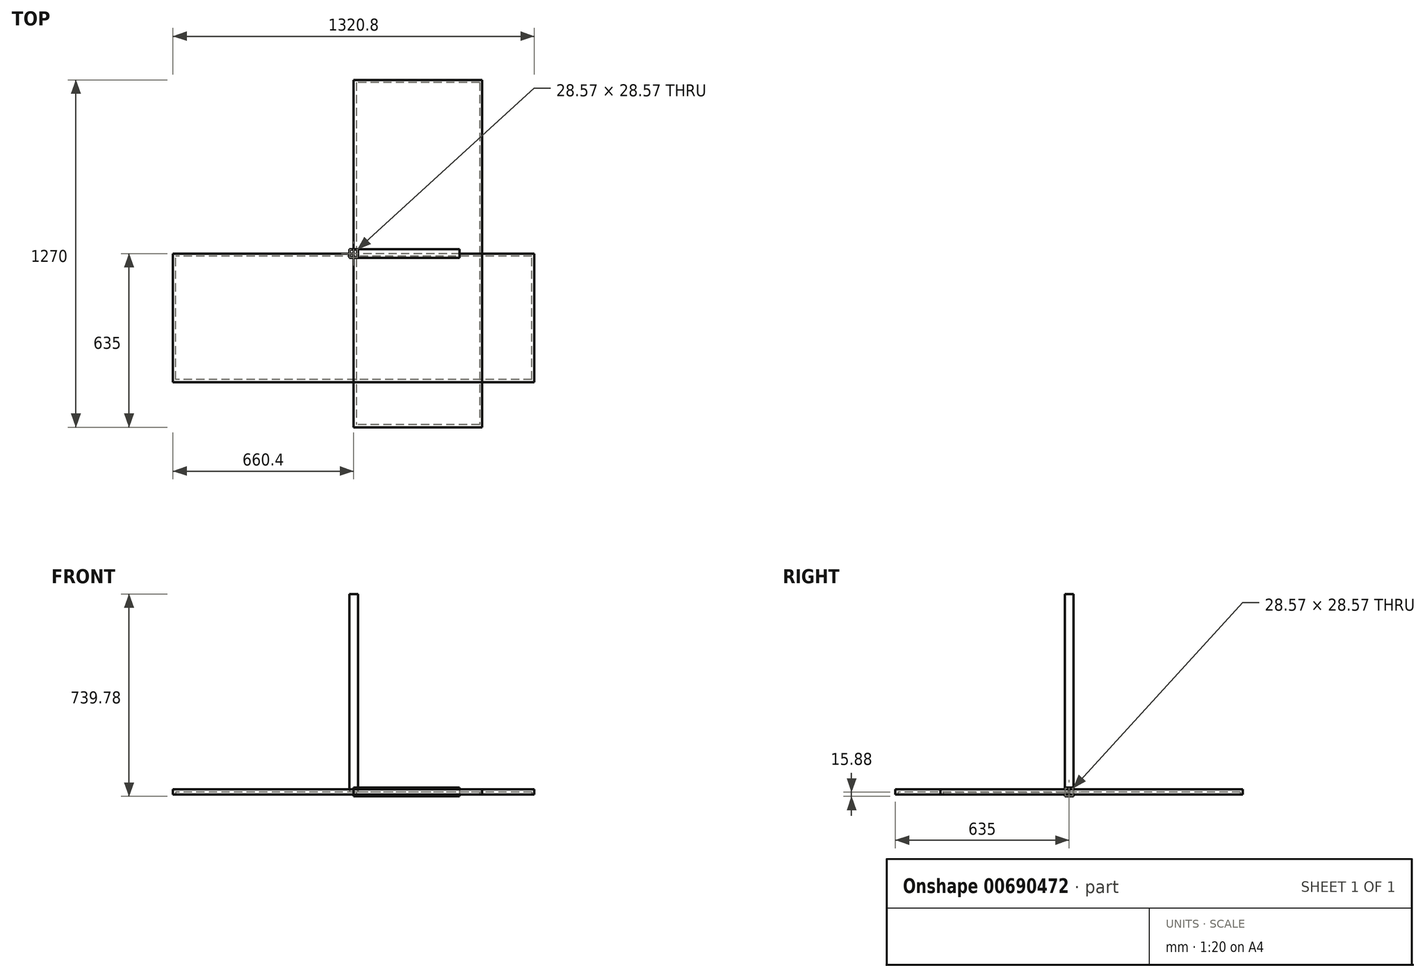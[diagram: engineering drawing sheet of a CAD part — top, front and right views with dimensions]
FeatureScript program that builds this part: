
annotation { "Feature Type Name" : "Feature", "Feature Type Description" : "" }
export const myFeature = defineFeature(function(context is Context, id is Id, definition is map)
    precondition{}
    {
        {
            var Q0;
            Q0=qCreatedBy(makeId("Front.planeOp"),FACE);
            var sketch = newSketch(context, id + "F0", { "sketchPlane" : qUnion([Q0])});
            skLineSegment(sketch, "E0.bottom", {"start": v(660.4, 9.52) * mm, "end": v(-660.4, 9.52) * mm});
            skLineSegment(sketch, "E0.top", {"start": v(650.88, -9.53) * mm, "end": v(-660.4, -9.53) * mm});
            skLineSegment(sketch, "E0.left", {"start": v(660.4, 9.52) * mm, "end": v(660.4, 0) * mm});
            skLineSegment(sketch, "E0.right", {"start": v(-660.4, 9.52) * mm, "end": v(-660.4, -9.53) * mm});
            skPoint(sketch, "E0.middle", {"position": v(0, 0) * mm});
            skPoint(sketch, "E1.orphan", {"position": v(660.4, -9.53) * mm});
            skLineSegment(sketch, "E2", {"start": v(650.88, -9.53) * mm, "end": v(660.4, -9.53) * mm});
            skLineSegment(sketch, "E3", {"start": v(660.4, 0) * mm, "end": v(660.4, -9.53) * mm});
            skSolve(sketch);
        }
        {
            var Q0;
            Q0 = qSketchRegion(id + "F0", true);
            extrude(context, id + "F1", {"entities" : qUnion([Q0]), "depth" : 469.9 * mm, "offsetDistance" : 25.4 * mm});
        }
        {
            var Q0;
            Q0=qCreatedBy(makeId("Right.planeOp"),FACE);
            var sketch = newSketch(context, id + "F2", { "sketchPlane" : qUnion([Q0])});
            skLineSegment(sketch, "E4.bottom", {"start": v(635, 9.53) * mm, "end": v(-635, 9.53) * mm});
            skLineSegment(sketch, "E4.top", {"start": v(635, -9.53) * mm, "end": v(-635, -9.53) * mm});
            skLineSegment(sketch, "E4.left", {"start": v(635, 9.52) * mm, "end": v(635, -9.53) * mm});
            skLineSegment(sketch, "E4.right", {"start": v(-635, 9.53) * mm, "end": v(-635, -9.53) * mm});
            skPoint(sketch, "E4.middle", {"position": v(0, 0) * mm});
            skLineSegment(sketch, "E5", {"start": v(-635, 9.53) * mm, "end": v(-165.1, 9.53) * mm});
            skLineSegment(sketch, "E6", {"start": v(-165.1, 9.53) * mm, "end": v(-165.1, 9.53) * mm});
            skLineSegment(sketch, "E7", {"start": v(-635, 9.53) * mm, "end": v(-635, 0) * mm});
            skLineSegment(sketch, "E8", {"start": v(-165.1, 9.53) * mm, "end": v(-165.1, 0) * mm});
            skLineSegment(sketch, "E9", {"start": v(-635, 0) * mm, "end": v(-165.1, 0) * mm});
            skSolve(sketch);
        }
        {
            var Q0;
            Q0 = qSketchRegion(id + "F2", true);
            extrude(context, id + "F3", {"entities" : qUnion([Q0]), "depth" : 469.9 * mm, "offsetDistance" : 25.4 * mm});
        }
        {
            var Q0;
            Q0=makeQuery(id+"F1.opExtrude","SWEPT_FACE",FACE,{"disambiguationData":[OSD([sQuery(id+"F0.wireOp",EDGE,"E0.top"),sQuery(id+"F0.wireOp",EDGE,"E2")])]});
            shell(context, id + "F4", {"entities" : qUnion([Q0]), "thickness" : 9.52 * mm});
        }
        {
            var Q0;
            Q0=makeQuery(id+"F3.opExtrude","SWEPT_FACE",FACE,{"disambiguationData":[OSD([sQuery(id+"F2.wireOp",EDGE,"E4.top")])]});
            var Q1;
            Q1=makeQuery(id+"F3.opExtrude","SWEPT_BODY",BODY,{"disambiguationData":[OSD([sQuery(id+"F2.wireOp",EDGE,"E4.bottom"),sQuery(id+"F2.wireOp",EDGE,"E4.top"),sQuery(id+"F2.wireOp",EDGE,"E4.left"),sQuery(id+"F2.wireOp",EDGE,"E4.right"),sQuery(id+"F2.wireOp",EDGE,"E5"),sQuery(id+"F2.wireOp",EDGE,"E7")])]});
            shell(context, id + "F5", {"entities" : qUnion([Q0]), "parts" : qUnion([Q1]), "thickness" : 9.52 * mm});
        }
        {
            var Q0;
            Q0=qCreatedBy(makeId("Top.planeOp"),FACE);
            var sketch = newSketch(context, id + "F6", { "sketchPlane" : qUnion([Q0])});
            skLineSegment(sketch, "E10.bottom", {"start": v(15.88, 15.88) * mm, "end": v(-15.88, 15.87) * mm});
            skLineSegment(sketch, "E10.top", {"start": v(15.88, -15.87) * mm, "end": v(-15.88, -15.88) * mm});
            skLineSegment(sketch, "E10.left", {"start": v(15.88, 15.88) * mm, "end": v(15.88, -15.87) * mm});
            skLineSegment(sketch, "E10.right", {"start": v(-15.88, 15.87) * mm, "end": v(-15.88, -15.88) * mm});
            skPoint(sketch, "E10.middle", {"position": v(0, 0) * mm});
            skLineSegment(sketch, "E11.bottom", {"start": v(14.29, 14.29) * mm, "end": v(-14.29, 14.29) * mm});
            skLineSegment(sketch, "E11.top", {"start": v(14.29, -14.29) * mm, "end": v(-14.29, -14.29) * mm});
            skLineSegment(sketch, "E11.left", {"start": v(14.29, 14.29) * mm, "end": v(14.29, -14.29) * mm});
            skLineSegment(sketch, "E11.right", {"start": v(-14.29, 14.29) * mm, "end": v(-14.29, -14.29) * mm});
            skSolve(sketch);
        }
        {
            var Q0;
            Q0 = qSketchRegion(id + "F6", true);
            extrude(context, id + "F7", {"entities" : qUnion([Q0]), "depth" : 723.9 * mm, "offsetDistance" : 25.4 * mm});
        }
        {
            var Q0;
            Q0=qCreatedBy(makeId("Right.planeOp"),FACE);
            var sketch = newSketch(context, id + "F8", { "sketchPlane" : qUnion([Q0])});
            skLineSegment(sketch, "E12.bottom", {"start": v(15.87, 15.88) * mm, "end": v(-15.88, 15.87) * mm});
            skLineSegment(sketch, "E12.top", {"start": v(15.88, -15.87) * mm, "end": v(-15.87, -15.88) * mm});
            skLineSegment(sketch, "E12.left", {"start": v(15.87, 15.88) * mm, "end": v(15.88, -15.87) * mm});
            skLineSegment(sketch, "E12.right", {"start": v(-15.88, 15.87) * mm, "end": v(-15.87, -15.88) * mm});
            skPoint(sketch, "E12.middle", {"position": v(0, 0) * mm});
            skLineSegment(sketch, "E13.bottom", {"start": v(14.29, 14.29) * mm, "end": v(-14.29, 14.29) * mm});
            skLineSegment(sketch, "E13.top", {"start": v(14.29, -14.29) * mm, "end": v(-14.29, -14.29) * mm});
            skLineSegment(sketch, "E13.left", {"start": v(14.29, 14.29) * mm, "end": v(14.29, -14.29) * mm});
            skLineSegment(sketch, "E13.right", {"start": v(-14.29, 14.29) * mm, "end": v(-14.29, -14.29) * mm});
            skSolve(sketch);
        }
        {
            var Q0;
            Q0 = qSketchRegion(id + "F8", true);
            extrude(context, id + "F9", {"entities" : qUnion([Q0]), "depth" : 387.35 * mm, "offsetDistance" : 25.4 * mm});
        }
    });
